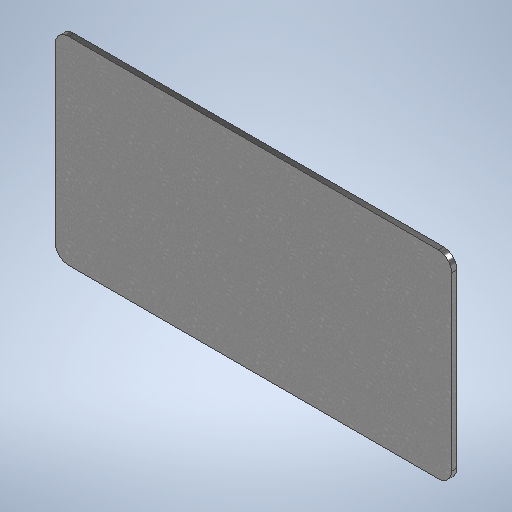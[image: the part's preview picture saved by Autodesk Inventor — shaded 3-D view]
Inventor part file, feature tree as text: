
AUTODESK INVENTOR PART (.ipt)
format: ipt  version: 2025.2 (Build 292293000, 293)  size: 295,424 bytes
history: native  units: mm
features: fillet x3, other x2, sheet_metal_op x1, sketch x1
ambient origin geometry x8: Origin, YZ Plane, XZ Plane, XY Plane, X Axis, Y Axis, Z Axis, Center Point
bodies: Body1 (feature_tree)
feature tree (7):
  other  "Sólido1"
  sheet_metal_op  "Face1"
  fillet  "Arredondamento1"  Radius=1500.0mm
  fillet  "Arredondamento2"  Radius=750.0mm
  fillet  "Arredondamento3"  Radius=20.0mm
  sketch  "Esboço1"  dims[d3=50.0mm d4=50.0mm d5=50.0mm]
  other  "Placa1"
